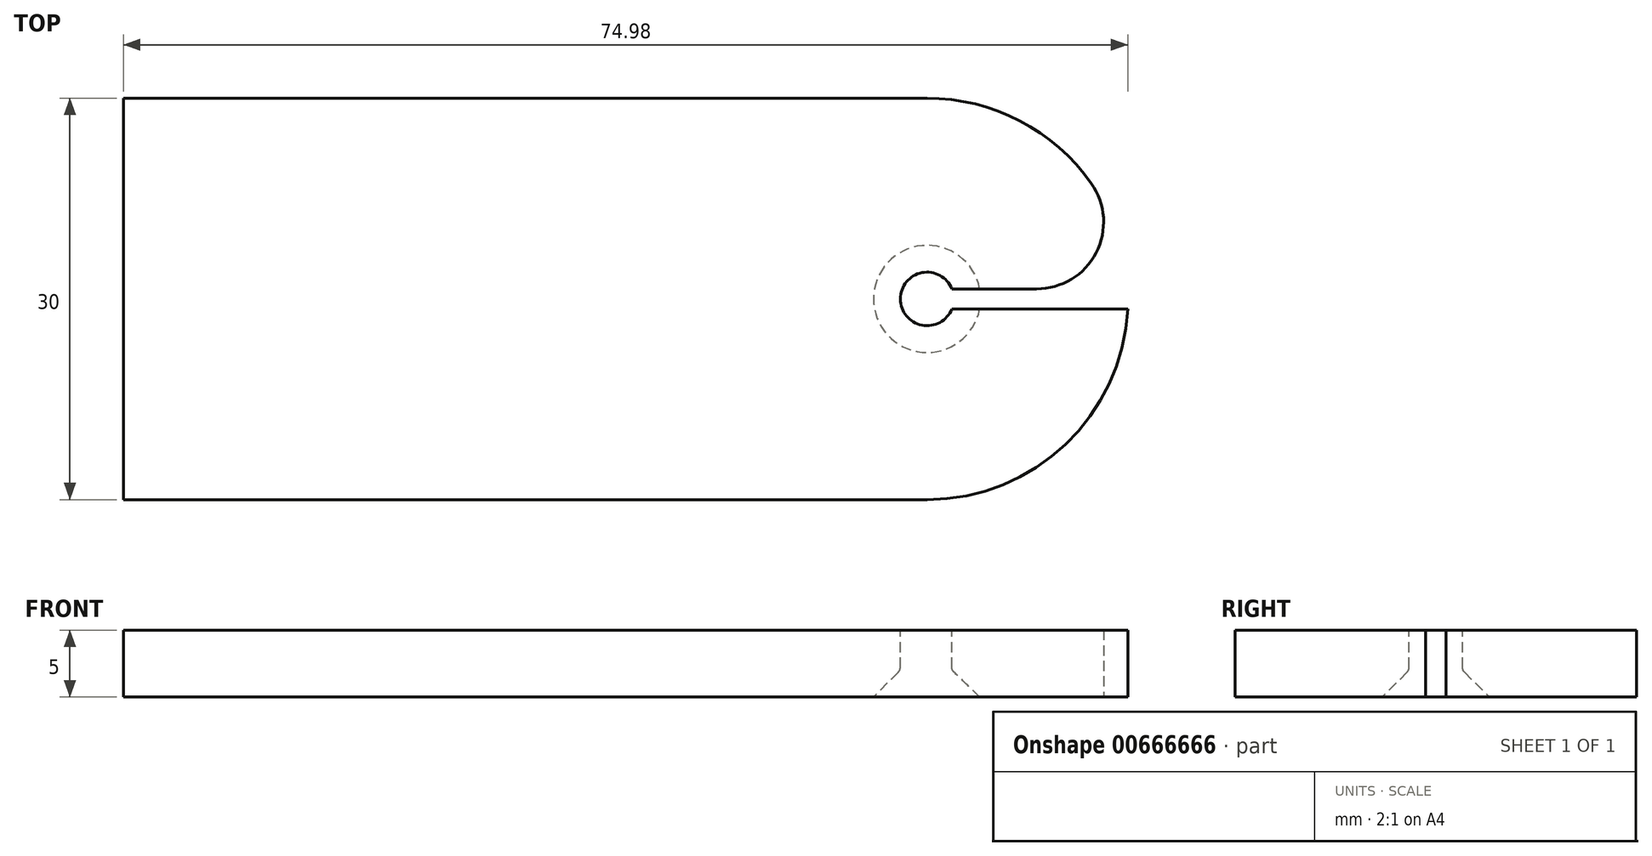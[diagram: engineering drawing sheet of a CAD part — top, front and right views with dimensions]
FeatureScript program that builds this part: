
annotation { "Feature Type Name" : "Feature", "Feature Type Description" : "" }
export const myFeature = defineFeature(function(context is Context, id is Id, definition is map)
    precondition{}
    {
        {
            var Q0;
            Q0=qCreatedBy(makeId("Top.planeOp"),FACE);
            var sketch = newSketch(context, id + "F0", { "sketchPlane" : qUnion([Q0])});
            skLineSegment(sketch, "E0", {"start": v(-26.73, 0) * mm, "end": v(-26.73, 15) * mm});
            skLineSegment(sketch, "E1", {"start": v(-26.73, 15) * mm, "end": v(33.27, 15) * mm});
            skLineSegment(sketch, "E2", {"start": v(-26.73, 0) * mm, "end": v(-26.73, -15) * mm});
            skLineSegment(sketch, "E3", {"start": v(-26.73, -15) * mm, "end": v(33.27, -15) * mm});
            skArc(sketch, "E4", {"start": v(33.27, -15) * mm, "mid": v(48.27, 0) * mm, "end": v(33.27, 15) * mm});
            skSolve(sketch);
        }
        {
            var Q0;
            Q0=makeQuery(id+"F0.imprint","IMPRINT",FACE,{"disambiguationData":[TD([[makeQuery(id+"F0.imprint","IMPRINT",EDGE,{"derivedFrom":sQuery(id+"F0.wireOp",EDGE,"E0")}),-1.0]])]});
            extrude(context, id + "F1", {"entities" : qUnion([Q0]), "depth" : 5 * mm, "offsetDistance" : 25 * mm});
        }
        {
            var Q0;
            Q0=makeQuery(id+"F1.opExtrude","CAP_FACE",FACE,{"disambiguationData":[OSD([sQuery(id+"F0.wireOp",EDGE,"E0"),sQuery(id+"F0.wireOp",EDGE,"E1"),sQuery(id+"F0.wireOp",EDGE,"E2"),sQuery(id+"F0.wireOp",EDGE,"E3"),sQuery(id+"F0.wireOp",EDGE,"E4")])],"isStart":false});
            var sketch = newSketch(context, id + "F2", { "sketchPlane" : qUnion([Q0])});
            skLineSegment(sketch, "E5.bottom", {"start": v(63.27, -0.75) * mm, "end": v(33.27, -0.75) * mm});
            skLineSegment(sketch, "E5.top", {"start": v(63.27, 0.75) * mm, "end": v(33.27, 0.75) * mm});
            skLineSegment(sketch, "E5.left", {"start": v(63.27, -0.75) * mm, "end": v(63.27, 0.75) * mm});
            skLineSegment(sketch, "E5.right", {"start": v(33.27, -0.75) * mm, "end": v(33.27, 0.75) * mm});
            skPoint(sketch, "E5.middle", {"position": v(48.27, 0) * mm});
            skCircle(sketch, "E6", {"center": v(33.27, 0) * mm, "radius": 2 * mm});
            skSolve(sketch);
        }
        {
            var Q0;
            {var subQ0=sQuery(id+"F2.wireOp",EDGE,"E6");var subQ1=sQuery(id+"F2.wireOp",EDGE,"E5.bottom");var subQ2=makeQuery(id+"F2.imprint","INTERSECT",VERTEX,{"derivedFrom":[subQ1,subQ0]});Q0=makeQuery(id+"F2.imprint","IMPRINT",FACE,{"disambiguationData":[TD([[makeQuery(id+"F2.imprint","IMPRINT",EDGE,{"disambiguationData":[TD([[subQ2,1.0]])],"derivedFrom":subQ1}),-1.0]])]});}
            var Q1;
            {var subQ0=sQuery(id+"F2.wireOp",EDGE,"E5.right");Q1=makeQuery(id+"F2.imprint","IMPRINT",FACE,{"disambiguationData":[TD([[makeQuery(id+"F2.imprint","IMPRINT",EDGE,{"derivedFrom":subQ0}),1.0]])]});}
            var Q2;
            {var subQ0=sQuery(id+"F2.wireOp",EDGE,"E5.right");Q2=makeQuery(id+"F2.imprint","IMPRINT",FACE,{"disambiguationData":[TD([[makeQuery(id+"F2.imprint","IMPRINT",EDGE,{"derivedFrom":subQ0}),-1.0]])]});}
            extrude(context, id + "F3", {"entities" : qUnion([Q0, Q1, Q2]), "operationType" : NewBodyOperationType.REMOVE, "endBound" : BoundingType.THROUGH_ALL, "oppositeDirection" : true, "depth" : mm, "offsetDistance" : 25 * mm});
        }
        {
            var Q0;
            Q0=makeQuery(id+"F3.boolean.opBoolean","COPY",EDGE,{"derivedFrom":makeQuery(id+"F3.opExtrude","CAP_EDGE",EDGE,{"disambiguationData":[OSD([sQuery(id+"F2.wireOp",EDGE,"E6")])],"isStart":true})});
            var Q1;
            Q1=makeQuery(id+"F3.boolean.opBoolean","INTERSECT",EDGE,{"derivedFrom":[makeQuery(id+"F1.opExtrude","CAP_FACE",FACE,{"disambiguationData":[OSD([sQuery(id+"F0.wireOp",EDGE,"E0"),sQuery(id+"F0.wireOp",EDGE,"E1"),sQuery(id+"F0.wireOp",EDGE,"E2"),sQuery(id+"F0.wireOp",EDGE,"E3"),sQuery(id+"F0.wireOp",EDGE,"E4")])],"isStart":true}),makeQuery(id+"F3.opExtrude","SWEPT_FACE",FACE,{"disambiguationData":[OSD([sQuery(id+"F2.wireOp",EDGE,"E6")])]})]});
            chamfer(context, id + "F4", {"entities" : qUnion([Q0, Q1]), "width" : 2 * mm, "tangentPropagation" : true});
        }
        {
            var Q0;
            {var subQ0=sQuery(id+"F2.wireOp",EDGE,"E6");Q0=makeQuery(id+"F4.opChamfer","BLEND_EDGE",EDGE,{"blendedFrom":[makeQuery(id+"F3.boolean.opBoolean","COPY",EDGE,{"derivedFrom":makeQuery(id+"F3.opExtrude","CAP_EDGE",EDGE,{"disambiguationData":[OSD([subQ0])],"isStart":true})}),makeQuery(id+"F3.boolean.opBoolean","COPY",FACE,{"derivedFrom":makeQuery(id+"F3.opExtrude","SWEPT_FACE",FACE,{"disambiguationData":[OSD([subQ0])]})})],"blendedInto":[makeQuery(id+"F3.boolean.opBoolean","COPY",FACE,{"derivedFrom":makeQuery(id+"F3.opExtrude","SWEPT_FACE",FACE,{"disambiguationData":[OSD([subQ0])]})})]});}
            var Q1;
            {var subQ0=makeQuery(id+"F3.opExtrude","SWEPT_FACE",FACE,{"disambiguationData":[OSD([sQuery(id+"F2.wireOp",EDGE,"E6")])]});Q1=makeQuery(id+"F4.opChamfer","BLEND_EDGE",EDGE,{"blendedFrom":[makeQuery(id+"F3.boolean.opBoolean","INTERSECT",EDGE,{"derivedFrom":[makeQuery(id+"F1.opExtrude","CAP_FACE",FACE,{"disambiguationData":[OSD([sQuery(id+"F0.wireOp",EDGE,"E0"),sQuery(id+"F0.wireOp",EDGE,"E1"),sQuery(id+"F0.wireOp",EDGE,"E2"),sQuery(id+"F0.wireOp",EDGE,"E3"),sQuery(id+"F0.wireOp",EDGE,"E4")])],"isStart":true}),subQ0]}),makeQuery(id+"F3.boolean.opBoolean","COPY",FACE,{"derivedFrom":subQ0})],"blendedInto":[makeQuery(id+"F3.boolean.opBoolean","COPY",FACE,{"derivedFrom":subQ0})]});}
            fillet(context, id + "F5", {"entities" : qUnion([Q0, Q1]), "radius" : 0.5 * mm, "tangentPropagation" : true, "allowEdgeOverflow" : false});
        }
        {
            var Q0;
            Q0=makeQuery(id+"F3.boolean.opBoolean","COPY",EDGE,{"derivedFrom":makeQuery(id+"F3.opExtrude","SWEPT_EDGE",EDGE,{"disambiguationData":[OSD([sQuery(id+"F0.wireOp",EDGE,"E4"),sQuery(id+"F2.wireOp",EDGE,"E5.top")])]})});
            var Q1;
            Q1=makeQuery(id+"F3.boolean.opBoolean","COPY",EDGE,{"derivedFrom":makeQuery(id+"F3.opExtrude","SWEPT_EDGE",EDGE,{"disambiguationData":[OSD([sQuery(id+"F0.wireOp",EDGE,"E4"),sQuery(id+"F2.wireOp",EDGE,"E5.bottom")])]})});
            fillet(context, id + "F6", {"entities" : qUnion([Q0, Q1]), "radius" : 5 * mm, "tangentPropagation" : true, "allowEdgeOverflow" : false});
        }
    });
